# Revit family: Урна стальная «Арго» Арт 19648
name_source: partatom
category: Антураж
revit_build: Autodesk Revit 2018 (Build: 20180423_1000(x64)
units: mm (PartAtom-declared; Revit-internal decimal feet)

## family parameters
Всегда вертикально = Да
Источник визуального образа = Геометрия семейства
На основе рабочей плоскости = Нет
Общий = Нет
При загрузке вырезать с полостями = Нет
Точка расчета площади = Нет

## types (2) — shared parameters
URL = https://hobbyka.ru
Артикул товара = Арт. 19648
Высота = 1050 мм
Группа модели = Уличные урны
Длина = 620 мм
Изготовитель = ООО «Хоббика»
Изображение типоразмера = Урна стальная «Арго» Арт 19648.jpg
Цвет урны = Сталь
Ширина = 470 мм

## per-type parameters (varying)
| type | Ангарская сосна | Композит | Материал изделия | Цвет отделки |
| Урна стальная «Арго». Версия «Ангарская сосна» | Да | Нет | Сталь, дерево | Ангарская сосна |
| Урна стальная «Арго». Версия «Композит» | Нет | Да | Сталь, композит | Композит |

note: column(s) folded — value = type name in every type: Описание
